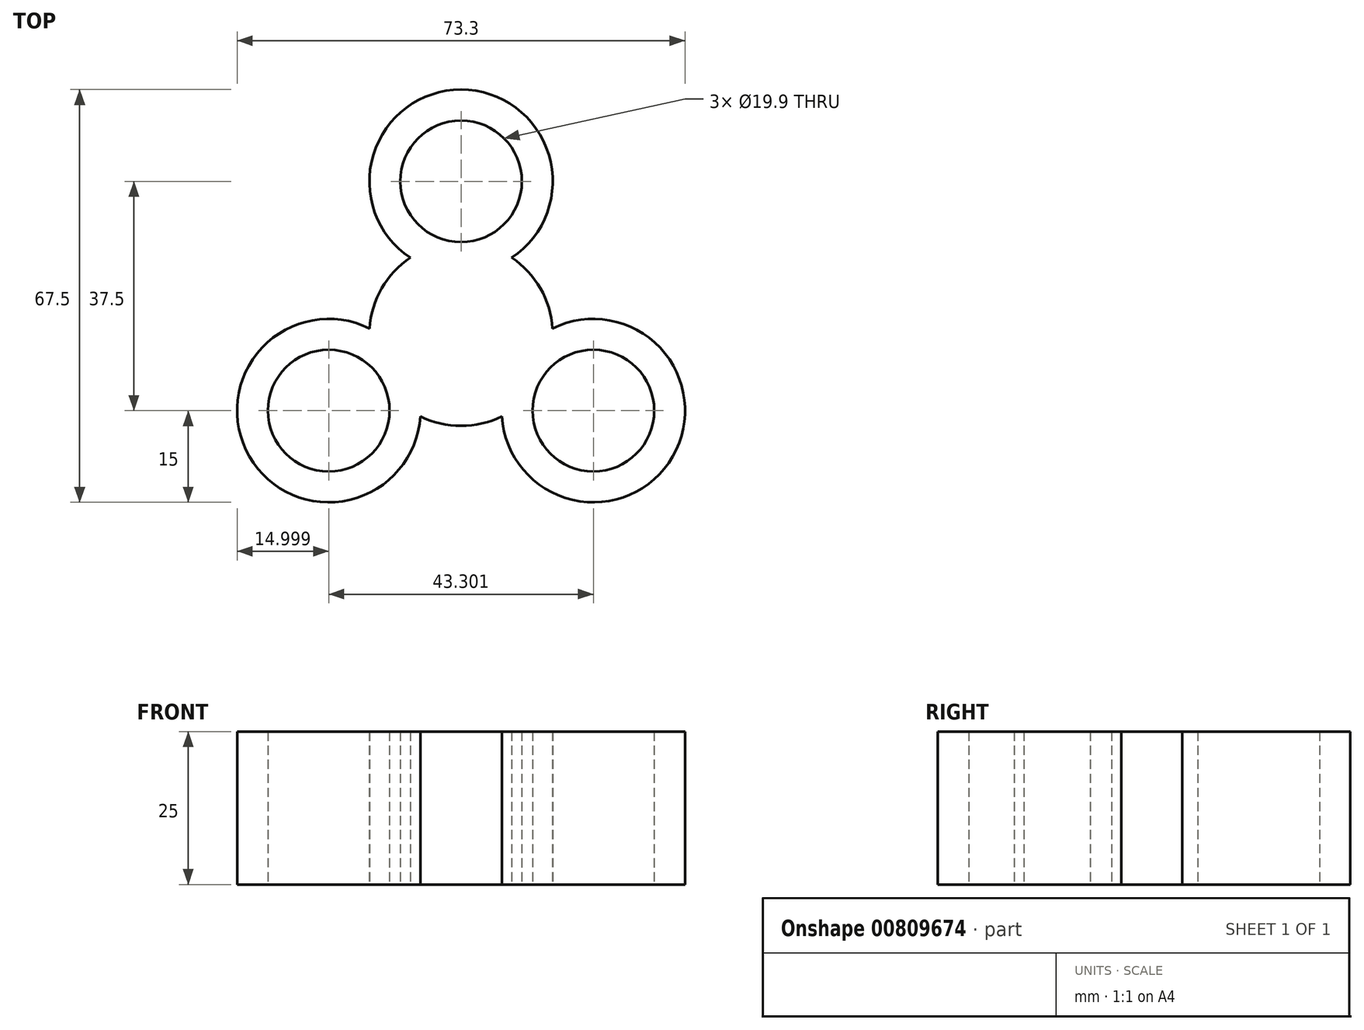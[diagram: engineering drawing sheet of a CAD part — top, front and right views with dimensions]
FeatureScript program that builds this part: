
annotation { "Feature Type Name" : "Feature", "Feature Type Description" : "" }
export const myFeature = defineFeature(function(context is Context, id is Id, definition is map)
    precondition{}
    {
        {
            var Q0;
            Q0=qCreatedBy(makeId("Top.planeOp"),FACE);
            var sketch = newSketch(context, id + "F0", { "sketchPlane" : qUnion([Q0])});
            skArc(sketch, "E0", {"start": v(9.34, 5.4) * mm, "mid": v(-0.05, 10.73) * mm, "end": v(-9.47, 5.47) * mm});
            skCircle(sketch, "E1", {"center": v(0, 25) * mm, "radius": 9.95 * mm});
            skArc(sketch, "E2", {"start": v(-8.3, 12.5) * mm, "mid": v(-10.93, 10.27) * mm, "end": v(-13, 7.5) * mm});
            skArc(sketch, "E3", {"start": v(8.3, 12.5) * mm, "mid": v(0, 40) * mm, "end": v(-8.3, 12.5) * mm});
            skArc(sketch, "E4.trimOffspring", {"start": v(13, 7.5) * mm, "mid": v(10.93, 10.27) * mm, "end": v(8.3, 12.5) * mm});
            skArc(sketch, "E5.1.0", {"start": v(-13, 7.5) * mm, "mid": v(-14.36, 4.33) * mm, "end": v(-14.97, 0.93) * mm});
            skArc(sketch, "E5.1.1", {"start": v(-6.68, -13.43) * mm, "mid": v(-3.43, -14.6) * mm, "end": v(0, -15) * mm});
            skArc(sketch, "E5.1.2", {"start": v(-14.97, 0.93) * mm, "mid": v(-34.64, -20) * mm, "end": v(-6.68, -13.43) * mm});
            skArc(sketch, "E5.1.3", {"start": v(-9.34, 5.4) * mm, "mid": v(-9.27, -5.4) * mm, "end": v(0, -10.94) * mm});
            skCircle(sketch, "E5.1.4", {"center": v(-21.65, -12.5) * mm, "radius": 9.95 * mm});
            skArc(sketch, "E5.2.0", {"start": v(0, -15) * mm, "mid": v(3.43, -14.6) * mm, "end": v(6.68, -13.43) * mm});
            skArc(sketch, "E5.2.1", {"start": v(14.97, 0.93) * mm, "mid": v(14.36, 4.33) * mm, "end": v(13, 7.5) * mm});
            skArc(sketch, "E5.2.2", {"start": v(6.68, -13.43) * mm, "mid": v(34.64, -20) * mm, "end": v(14.97, 0.93) * mm});
            skArc(sketch, "E5.2.3", {"start": v(0, -10.78) * mm, "mid": v(9.31, -5.32) * mm, "end": v(9.47, 5.47) * mm});
            skCircle(sketch, "E5.2.4", {"center": v(21.65, -12.5) * mm, "radius": 9.95 * mm});
            skSolve(sketch);
        }
        {
            var Q0;
            Q0 = qSketchRegion(id + "F0", true);
            extrude(context, id + "F1", {"entities" : qUnion([Q0]), "depth" : 25 * mm, "offsetDistance" : 25 * mm});
        }
    });
